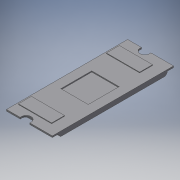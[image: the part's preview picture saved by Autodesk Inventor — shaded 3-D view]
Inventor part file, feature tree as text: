
AUTODESK INVENTOR PART (.ipt)
format: ipt  version: 2016 SP2 (Build 200236200, 236)  size: 198,656 bytes
history: native  units: mm
features: extrude x5, sketch x5, reference x3, chamfer x1
ambient origin geometry x8: Origin, YZ Plane, XZ Plane, XY Plane, X Axis, Y Axis, Z Axis, Center Point
bodies: Volumenkörper1 (feature_tree)
feature tree (14):
  extrude  "Extrusion1"  Depth=24.9mm
  extrude  "Extrusion2"  Depth=3.5mm
  extrude  "Extrusion3"  Depth=0.8mm TaperAngle=0.0deg
  chamfer  "Fase1"  Distance=7.0mm
  extrude  "Extrusion4"  Depth=7.0mm
  extrude  "Extrusion5"  Depth=5.5mm
  sketch  "Skizze1"  dims[d0=0.1mm d1=24.9mm]
  reference  "Referenz1"
  sketch  "Skizze2"  dims[d2=1.8mm d3=0.0mm d4=3.5mm]
  sketch  "Skizze3"  dims[d5=3.5mm d6=0.8mm d7=0.0mm]
  sketch  "Skizze4"  dims[d8=18.0mm]
  sketch  "Skizze5"  dims[d9=18.0mm d10=7.0mm d11=7.0mm d12=5.5mm d13=5.5mm d14=1.0mm d15=0.4mm d16=0.0mm d17=1.0mm d18=2.0mm d19=45.0deg d20=12.0mm d21=12.0mm d22=0.4mm d23=0.0mm d24=12.0mm d25=12.0mm d26=5.0mm d27=5.0mm d28=0.6mm d29=0.0mm d30=2.5mm d31=5.3mm d32=2.5mm d33=5.3mm]
  reference  "Referenz2"
  reference  "Referenz3"
